FCSTD DOCUMENT  (FreeCAD 0.19R24291 (Git))
Label: 2D-Model
License: All rights reserved
LicenseURL: http://en.wikipedia.org/wiki/All_rights_reserved
objects: App::FeaturePython×14, Part::Part2DObjectPython×9, Part::Feature×7, Part::FeaturePython×4, Sketcher::SketchObject×1
note: 21 computed .brp shape members not serialized (recipe doc carries the construction recipe); baked Part::Feature solids carry a one-line shape summary decoded from their .brp

FEATURE [Sketcher::SketchObject] Sketch  label="Basic_Link"
  FullyConstrained = false
  sketch-geometry (6):
    g0: ArcOfCircle CenterX=-40 CenterY=0 CenterZ=0 NormalX=0 NormalY=0 NormalZ=1 AngleXU=0 Radius=5.01431 StartAngle=1.5708 EndAngle=4.71239
    g1: ArcOfCircle CenterX=40 CenterY=0 CenterZ=0 NormalX=0 NormalY=0 NormalZ=1 AngleXU=0 Radius=5.01431 StartAngle=4.71239 EndAngle=7.85398
    g2: LineSegment StartX=-40 StartY=-5.01431 StartZ=0 EndX=40 EndY=-5.01431 EndZ=0
    g3: LineSegment StartX=-40 StartY=5.01431 StartZ=0 EndX=40 EndY=5.01431 EndZ=0
    g4: Circle CenterX=-40 CenterY=-0.014306 CenterZ=0 NormalX=0 NormalY=0 NormalZ=1 AngleXU=0 Radius=2.5
    g5: Circle CenterX=40 CenterY=0 CenterZ=0 NormalX=0 NormalY=0 NormalZ=1 AngleXU=0 Radius=2.5
  constraints (11):
    c: Tangent(g0,g3) = 1.5708
    c: Tangent(g0,g2) = -1.5708
    c: Tangent(g2,g1) = -1.5708
    c: Tangent(g3,g1) = 1.5708
    c: Horizontal(g2)
    c: Equal(g0,g1)
    c: Distance(g-1,g1) = 40
    c: Distance(g-1,g0) = 40
    c: Coincident(g5,g1)
    c: Radius(g5) = 2.5
    c: Radius(g4) = 2.5
FEATURE [Part::FeaturePython] Connect001  label="Link_AR"  # WARN: FeaturePython — macro-defined, semantics opaque (R4)
  Objects = -> [Sketch]
  Placement = pos=(-52.53,37.12,0) rot=(0,0,1;1.91986rad)
  Tolerance = 0
FEATURE [Part::FeaturePython] Connect002  label="Link_BR"  # WARN: FeaturePython — macro-defined, semantics opaque (R4)
  Objects = -> [Sketch]
  Placement = pos=(-33.25,97,0) rot=(0,0,1;0.593412rad)
  Tolerance = 0
FEATURE [Part::FeaturePython] Connect004  label="Link_AL"  # WARN: FeaturePython — macro-defined, semantics opaque (R4)
  Objects = -> [Sketch]
  Placement = pos=(53.04,37.56,0) rot=(0,0,-1;1.91986rad)
  Tolerance = 0
FEATURE [Part::FeaturePython] Connect003  label="Link_BL"  # WARN: FeaturePython — macro-defined, semantics opaque (R4)
  Objects = -> [Sketch]
  Placement = pos=(33.25,97.5,0) rot=(0,0,-1;0.580322rad)
  Tolerance = 0
FEATURE [Part::Feature] Shape002  label="Link_BL_dashed_line"
  shape: bbox 60.94 x 41.1 x 2e-07 mm, 0 faces, 0 solids (baked)
FEATURE [Part::Feature] Shape003  label="Link_BR_dashed_line"
  shape: bbox 61.47 x 40.3 x 2e-07 mm, 0 faces, 0 solids (baked)
FEATURE [Part::Feature] Shape004  label="Link_AR_dashed_line"
  shape: bbox 37.1 x 102 x 2e-07 mm, 0 faces, 0 solids (baked)
FEATURE [Part::Feature] Shape005  label="Link_BR_dashed_line001"
  shape: bbox 37.86 x 104.9 x 2e-07 mm, 0 faces, 0 solids (baked)
FEATURE [Part::Part2DObjectPython] Line  # Draft 2D object (typed FeaturePython)
  Area = 0
  ChamferSize = 0
  Closed = false
  End = (-35.17,75.1156,0)
  FilletRadius = 0
  Length = 30
  MakeFace = true
  Placement = pos=(-66.165,75.1156,0) rot=(0,0,1;0rad)
  Points = (2) [(0.995031,-8.21533e-06,0),(30.995,9.17187e-08,0)]
  Start = (-65.17,75.1156,0)
  Subdivisions = 0
FEATURE [Part::Part2DObjectPython] Line001  # Draft 2D object (typed FeaturePython)
  Area = 0
  ChamferSize = 0
  Closed = true
  End = (96.17,75.1156,0)
  FilletRadius = 0
  Length = 30
  MakeFace = true
  Placement = pos=(-66.165,75.1156,0) rot=(0,0,1;0rad)
  Points = (2) [(132.335,-8.21533e-06,0),(162.335,-8.21533e-06,0)]
  Start = (66.17,75.1156,0)
  Subdivisions = 0
FEATURE [Part::Part2DObjectPython] Line002  # Draft 2D object (typed FeaturePython)
  Area = 0
  ChamferSize = 0
  Closed = false
  End = (80.8869,0,0)
  FilletRadius = 0
  Length = 119.745
  MakeFace = true
  Placement = pos=(-38.8586,-0.760523,0) rot=(0,0,1;0rad)
  Points = (2) [(-1.8457e-05,0.760523,0),(119.745,0.760523,0)]
  Start = (-38.8586,0,0)
  Subdivisions = 0
FEATURE [Part::Feature] Shape  label="utility_lines_base"
  shape: bbox 119.7 x 2e-07 x 2e-07 mm, 0 faces, 0 solids (baked)
FEATURE [Part::Feature] Shape007  label="utility_lines_R"
  shape: bbox 30 x 8.507e-06 x 2e-07 mm, 0 faces, 0 solids (baked)
FEATURE [Part::Feature] Shape008  label="utility_lines_L"
  shape: bbox 30 x 2e-07 x 2e-07 mm, 0 faces, 0 solids (baked)
FEATURE [Part::Part2DObjectPython] Arc  label="θ2andθ6"  # Draft 2D object (typed FeaturePython)
  Area = 0
  FirstAngle = 0.131411
  LastAngle = 110.131
  MakeFace = true
  Placement = pos=(-66.3249,75.0544,0) rot=(0,0,1;0rad)
  Radius = 19.7276
FEATURE [Part::Part2DObjectPython] Arc001  label="θ3minusθ7"  # Draft 2D object (typed FeaturePython)
  Area = 0
  FirstAngle = 0
  LastAngle = 71.1468
  MakeFace = true
  Placement = pos=(66.4224,75.0078,0) rot=(0,0,1;0rad)
  Radius = 19.8646
FEATURE [Part::Part2DObjectPython] Arc002  label="θ4"  # Draft 2D object (typed FeaturePython)
  Area = 0
  FirstAngle = 0.26649
  LastAngle = 70.1862
  MakeFace = true
  Placement = pos=(39.5119,-0.217988,0) rot=(0,0,1;0rad)
  Radius = 17.9346
FEATURE [Part::Part2DObjectPython] Arc003  label="θ1"  # Draft 2D object (typed FeaturePython)
  Area = 0
  FirstAngle = -0.451138
  LastAngle = 110.273
  MakeFace = true
  Placement = pos=(-38.9811,-0.0951508,0) rot=(0,0,1;0rad)
  Radius = 15.7126
FEATURE [App::FeaturePython] dLabel  label="θ1Label"  # WARN: FeaturePython — macro-defined, semantics opaque (R4)
  CustomText = \u03b81
  LabelType = 2
  Placement = pos=(-22.1234,15.1698,0) rot=(0,0,1;0rad)
  Points = (3) [(-22.1234,15.1698,0),(-26.376,15.1698,0),(-28.3904,11.8124,0)]
  StraightDirection = 0
  StraightDistance = -4.25266
  Target = -> Arc003 [Edge1]
  TargetPoint = (-28.3904,11.8124,0)
  Text = θ1
FEATURE [App::FeaturePython] dLabel001  label="θ4Label"  # WARN: FeaturePython — macro-defined, semantics opaque (R4)
  CustomText = Label
  LabelType = 2
  Placement = pos=(60.2439,14.0507,0) rot=(0,0,1;0rad)
  Points = (3) [(60.2439,14.0507,0),(56.2151,14.0507,0),(53.9768,10.2457,0)]
  StraightDirection = 0
  StraightDistance = -4.02884
  Target = -> Arc002 [Edge1]
  TargetPoint = (53.9768,10.2457,0)
  Text = θ4
FEATURE [Part::Part2DObjectPython] Arc004  label="θ2"  # Draft 2D object (typed FeaturePython)
  Area = 0
  FirstAngle = 1.48784
  LastAngle = 35.1807
  MakeFace = true
  Placement = pos=(-65.9929,74.707,0) rot=(0,0,1;0rad)
  Radius = 17.2403
FEATURE [App::FeaturePython] dLabel002  label="θ2Label"  # WARN: FeaturePython — macro-defined, semantics opaque (R4)
  CustomText = Label
  LabelType = 2
  Placement = pos=(-41.3722,79.6311,0) rot=(0,0,1;0rad)
  Points = (3) [(-41.3722,79.6311,0),(-45.1772,79.6311,0),(-48.7584,77.3929,0)]
  StraightDirection = 0
  StraightDistance = -3.80501
  Target = -> Arc004
  TargetPoint = (-48.7584,77.3929,0)
  Text = θ2
FEATURE [Part::Part2DObjectPython] Arc005  label="θ3"  # Draft 2D object (typed FeaturePython)
  Area = 0
  FirstAngle = 0.774192
  LastAngle = 143.616
  MakeFace = true
  Placement = pos=(66.2871,74.9308,0) rot=(0,0,1;0rad)
  Radius = 16.5645
FEATURE [App::FeaturePython] dLabel003  label="θ3Label"  # WARN: FeaturePython — macro-defined, semantics opaque (R4)
  CustomText = Label
  LabelType = 2
  Placement = pos=(90.4601,81.6455,0) rot=(0,0,1;0rad)
  Points = (3) [(90.4601,81.6455,0),(86.4313,81.6455,0),(82.4025,79.4073,0)]
  StraightDirection = 0
  StraightDistance = -4.02883
  Target = -> Arc005
  TargetPoint = (82.4025,79.4073,0)
  Text = θ3
FEATURE [App::FeaturePython] Text  label="EndEffector_Label"  # WARN: FeaturePython — macro-defined, semantics opaque (R4)
  Placement = pos=(-3,125.5,0) rot=(0,0,1;0rad)
  Text = E
FEATURE [App::FeaturePython] Text001  label="LinkA1_Label"  # WARN: FeaturePython — macro-defined, semantics opaque (R4)
  Placement = pos=(-65.53,29.8977,0) rot=(0,0,1;0rad)
  Text = La
FEATURE [App::FeaturePython] Text002  label="LinkA2_Label"  # WARN: FeaturePython — macro-defined, semantics opaque (R4)
  Placement = pos=(58.53,29.8977,0) rot=(0,0,1;0rad)
  Text = La
FEATURE [App::FeaturePython] Text003  label="LinkB1_Label"  # WARN: FeaturePython — macro-defined, semantics opaque (R4)
  Placement = pos=(-47,99.9,0) rot=(0,0,1;0rad)
  Text = Lb
FEATURE [App::FeaturePython] Text004  label="LinkB2_Label"  # WARN: FeaturePython — macro-defined, semantics opaque (R4)
  Placement = pos=(44,99.9,0) rot=(0,0,1;0rad)
  Text = Lb
FEATURE [App::FeaturePython] Text005  label="JoinA1_Label"  # WARN: FeaturePython — macro-defined, semantics opaque (R4)
  Placement = pos=(-54,-4,0) rot=(0,0,1;0rad)
  Text = A1
FEATURE [App::FeaturePython] Text006  label="JoinA2_Label"  # WARN: FeaturePython — macro-defined, semantics opaque (R4)
  Placement = pos=(46,-4,0) rot=(0,0,1;0rad)
  Text = A2
FEATURE [App::FeaturePython] Text007  label="JointB1_Label"  # WARN: FeaturePython — macro-defined, semantics opaque (R4)
  Placement = pos=(-81,72,0) rot=(0,0,1;0rad)
  Text = B1
FEATURE [App::FeaturePython] Text008  label="JointB2_Label"  # WARN: FeaturePython — macro-defined, semantics opaque (R4)
  Placement = pos=(73,72,0) rot=(0,0,1;0rad)
  Text = B2
FEATURE [App::FeaturePython] Text009  label="Signature_CL"  # WARN: FeaturePython — macro-defined, semantics opaque (R4)
  Placement = pos=(71.8138,-12.6659,0) rot=(0,0,1;0rad)
  Text = Chiara Leonori
